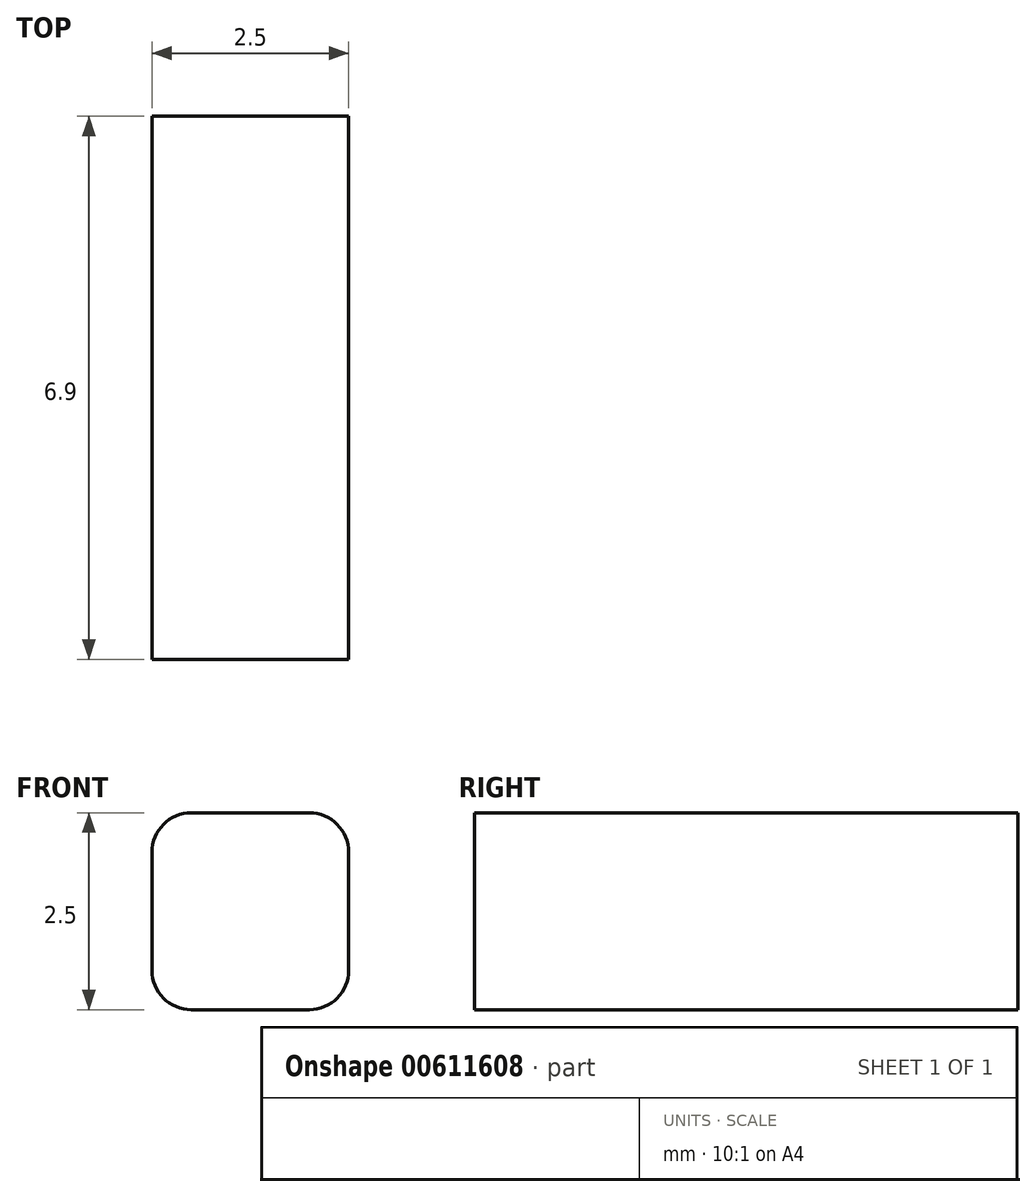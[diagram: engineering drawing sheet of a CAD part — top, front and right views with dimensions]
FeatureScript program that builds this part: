
annotation { "Feature Type Name" : "Feature", "Feature Type Description" : "" }
export const myFeature = defineFeature(function(context is Context, id is Id, definition is map)
    precondition{}
    {
        {
            var Q0;
            Q0=qCreatedBy(makeId("Front.planeOp"),FACE);
            var sketch = newSketch(context, id + "F0", { "sketchPlane" : qUnion([Q0])});
            skLineSegment(sketch, "E0.bottom", {"start": v(2.54, 5.04) * mm, "end": v(5.04, 5.04) * mm});
            skLineSegment(sketch, "E0.top", {"start": v(2.54, 2.54) * mm, "end": v(5.04, 2.54) * mm});
            skLineSegment(sketch, "E0.left", {"start": v(2.54, 5.04) * mm, "end": v(2.54, 2.54) * mm});
            skLineSegment(sketch, "E0.right", {"start": v(5.04, 5.04) * mm, "end": v(5.04, 2.54) * mm});
            skSolve(sketch);
        }
        {
            var Q0;
            Q0 = qSketchRegion(id + "F0", true);
            extrude(context, id + "F1", {"entities" : qUnion([Q0]), "depth" : 6.9 * mm, "offsetDistance" : 25 * mm});
        }
        {
            var Q0;
            Q0=makeQuery(id+"F1.opExtrude","SWEPT_EDGE",EDGE,{"disambiguationData":[OSD([sQuery(id+"F0.wireOp",EDGE,"E0.bottom"),sQuery(id+"F0.wireOp",EDGE,"E0.right")])]});
            var Q1;
            Q1=makeQuery(id+"F1.opExtrude","SWEPT_EDGE",EDGE,{"disambiguationData":[OSD([sQuery(id+"F0.wireOp",EDGE,"E0.top"),sQuery(id+"F0.wireOp",EDGE,"E0.right")])]});
            var Q2;
            Q2=makeQuery(id+"F1.opExtrude","SWEPT_EDGE",EDGE,{"disambiguationData":[OSD([sQuery(id+"F0.wireOp",EDGE,"E0.bottom"),sQuery(id+"F0.wireOp",EDGE,"E0.left")])]});
            var Q3;
            Q3=makeQuery(id+"F1.opExtrude","SWEPT_EDGE",EDGE,{"disambiguationData":[OSD([sQuery(id+"F0.wireOp",EDGE,"E0.top"),sQuery(id+"F0.wireOp",EDGE,"E0.left")])]});
            fillet(context, id + "F2", {"entities" : qUnion([Q0, Q1, Q2, Q3]), "radius" : .5 * mm, "tangentPropagation" : true, "allowEdgeOverflow" : false});
        }
    });
